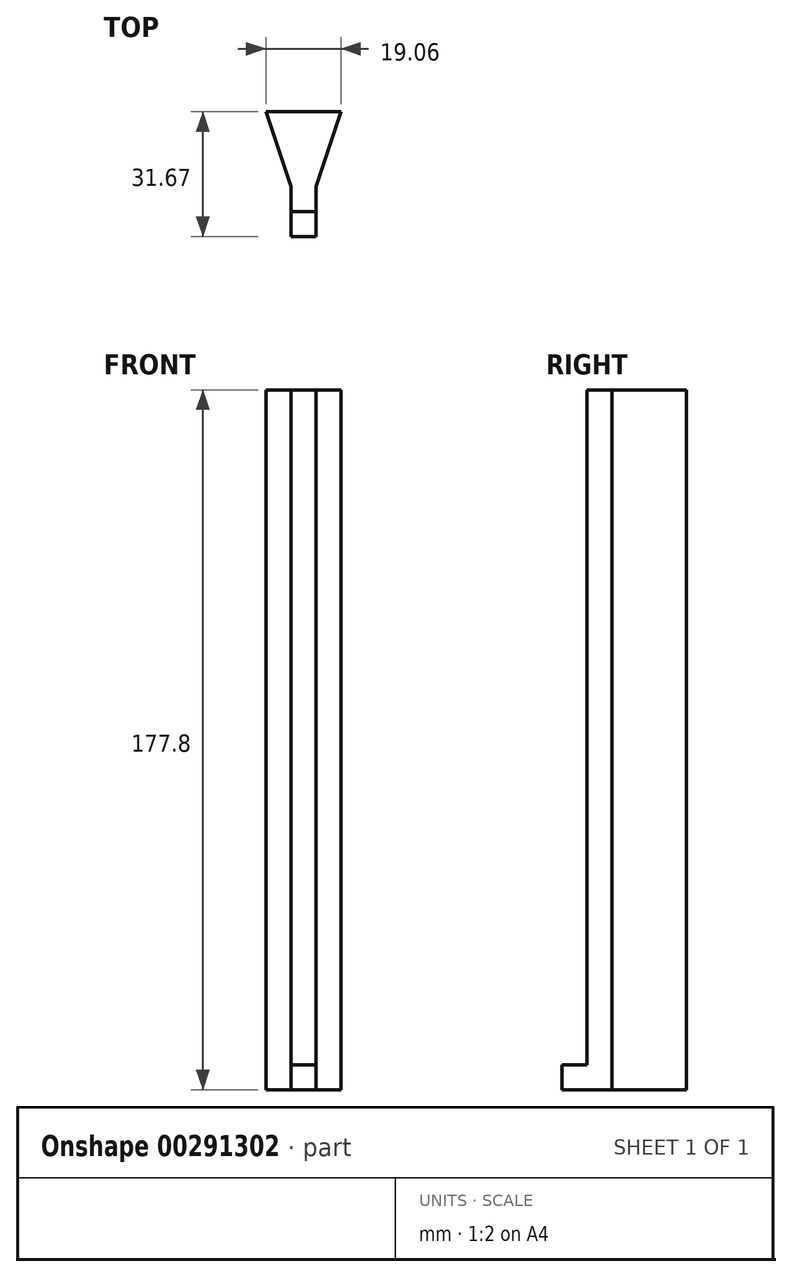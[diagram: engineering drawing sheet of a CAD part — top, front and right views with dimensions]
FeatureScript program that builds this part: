
annotation { "Feature Type Name" : "Feature", "Feature Type Description" : "" }
export const myFeature = defineFeature(function(context is Context, id is Id, definition is map)
    precondition{}
    {
        {
            var Q0;
            Q0=qCreatedBy(makeId("Top.planeOp"),FACE);
            var sketch = newSketch(context, id + "F0", { "sketchPlane" : qUnion([Q0])});
            skLineSegment(sketch, "E0", {"start": v(-9.52, -42.86) * mm, "end": v(9.53, -42.86) * mm});
            skLineSegment(sketch, "E1", {"start": v(9.53, -42.86) * mm, "end": v(3.18, -61.83) * mm});
            skLineSegment(sketch, "E2.MirrorCS", {"start": v(-9.52, -42.86) * mm, "end": v(-3.17, -61.83) * mm});
            skPoint(sketch, "E3.center", {"position": v(0, 0) * mm});
            skLineSegment(sketch, "E4.1.0", {"start": v(-3.18, -74.53) * mm, "end": v(3.17, -74.53) * mm});
            skLineSegment(sketch, "E5", {"start": v(-3.17, -61.83) * mm, "end": v(3.18, -61.83) * mm});
            skLineSegment(sketch, "E6", {"start": v(-3.17, -61.83) * mm, "end": v(-3.18, -74.53) * mm});
            skLineSegment(sketch, "E7", {"start": v(3.18, -61.83) * mm, "end": v(3.17, -74.53) * mm});
            skLineSegment(sketch, "E8", {"start": v(-3.18, -68.18) * mm, "end": v(3.17, -68.18) * mm});
            skSolve(sketch);
        }
        {
            var Q0;
            Q0=makeQuery(id+"F0.imprint","IMPRINT",FACE,{"disambiguationData":[TD([[makeQuery(id+"F0.imprint","IMPRINT",EDGE,{"derivedFrom":sQuery(id+"F0.wireOp",EDGE,"E0")}),-1.0]])]});
            var Q1;
            {var subQ0=sQuery(id+"F0.wireOp",EDGE,"E5");Q1=makeQuery(id+"F0.imprint","IMPRINT",FACE,{"disambiguationData":[TD([[makeQuery(id+"F0.imprint","IMPRINT",EDGE,{"derivedFrom":subQ0}),-1.0]])]});}
            extrude(context, id + "F1", {"entities" : qUnion([Q0, Q1]), "depth" : 177.8 * mm});
        }
        {
            var Q0;
            Q0=makeQuery(id+"F0.imprint","IMPRINT",FACE,{"disambiguationData":[TD([[makeQuery(id+"F0.imprint","IMPRINT",EDGE,{"derivedFrom":sQuery(id+"F0.wireOp",EDGE,"E4.1.0")}),1.0]])]});
            extrude(context, id + "F2", {"entities" : qUnion([Q0]), "operationType" : NewBodyOperationType.ADD, "depth" : 6.35 * mm});
        }
    });
